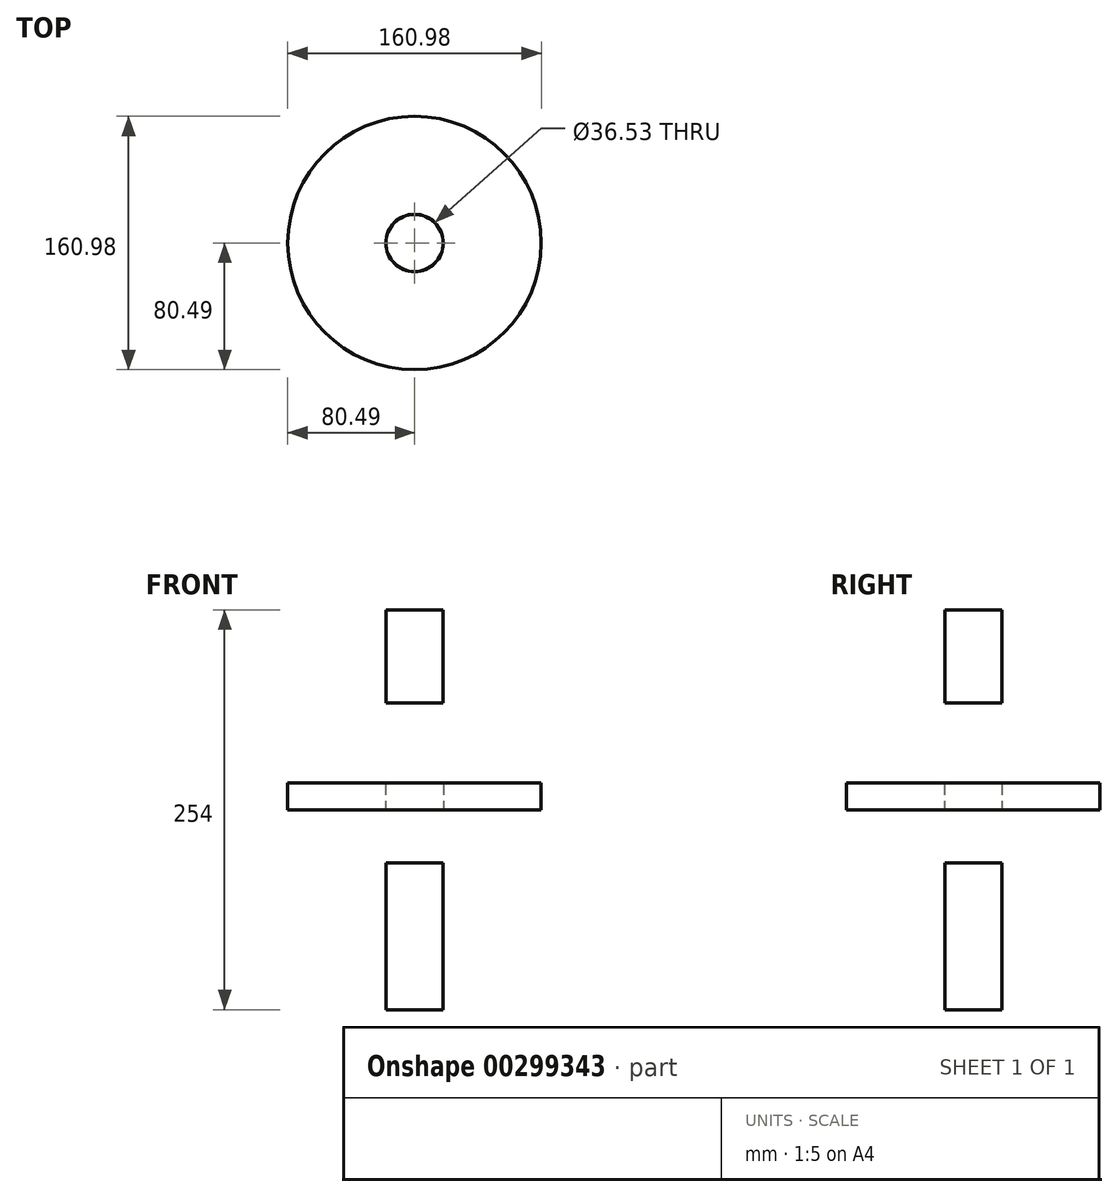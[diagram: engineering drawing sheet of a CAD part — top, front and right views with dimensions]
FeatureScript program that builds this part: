
annotation { "Feature Type Name" : "Feature", "Feature Type Description" : "" }
export const myFeature = defineFeature(function(context is Context, id is Id, definition is map)
    precondition{}
    {
        {
            var Q0;
            Q0=qCreatedBy(makeId("Top.planeOp"),FACE);
            var sketch = newSketch(context, id + "F0", { "sketchPlane" : qUnion([Q0])});
            skCircle(sketch, "E0", {"center": v(0, 0) * mm, "radius": 80.49 * mm});
            skSolve(sketch);
        }
        {
            var Q0;
            Q0 = qSketchRegion(id + "F0", true);
            extrude(context, id + "F1", {"entities" : qUnion([Q0]), "depth" : 17.02 * mm});
        }
        {
            var Q0;
            Q0=qCreatedBy(makeId("Top.planeOp"),FACE);
            var sketch = newSketch(context, id + "F2", { "sketchPlane" : qUnion([Q0])});
            skCircle(sketch, "E1", {"center": v(0, 0) * mm, "radius": 18.14 * mm});
            skSolve(sketch);
        }
        {
            var Q0;
            Q0=makeQuery(id+"F2.imprint","IMPRINT",FACE,{"disambiguationData":[TD([[makeQuery(id+"F2.imprint","IMPRINT",EDGE,{"derivedFrom":sQuery(id+"F2.wireOp",EDGE,"E1")}),1.0]])]});
            extrude(context, id + "F3", {"entities" : qUnion([Q0]), "depth" : 254 * mm, "symmetric" : true});
        }
        {
            var Q0;
            Q0=makeQuery(id+"F1.opExtrude","CAP_FACE",FACE,{"disambiguationData":[OSD([sQuery(id+"F0.wireOp",EDGE,"E0")])],"isStart":false});
            var sketch = newSketch(context, id + "F4", { "sketchPlane" : qUnion([Q0])});
            skCircle(sketch, "E2", {"center": v(0, 0) * mm, "radius": 18.26 * mm});
            skSolve(sketch);
        }
        {
            var Q0;
            Q0=makeQuery(id+"F4.imprint","IMPRINT",FACE,{"disambiguationData":[TD([[makeQuery(id+"F4.imprint","IMPRINT",EDGE,{"derivedFrom":sQuery(id+"F4.wireOp",EDGE,"E2")}),1.0]])]});
            extrude(context, id + "F5", {"entities" : qUnion([Q0]), "operationType" : NewBodyOperationType.REMOVE, "depth" : 101.6 * mm, "symmetric" : true});
        }
    });
